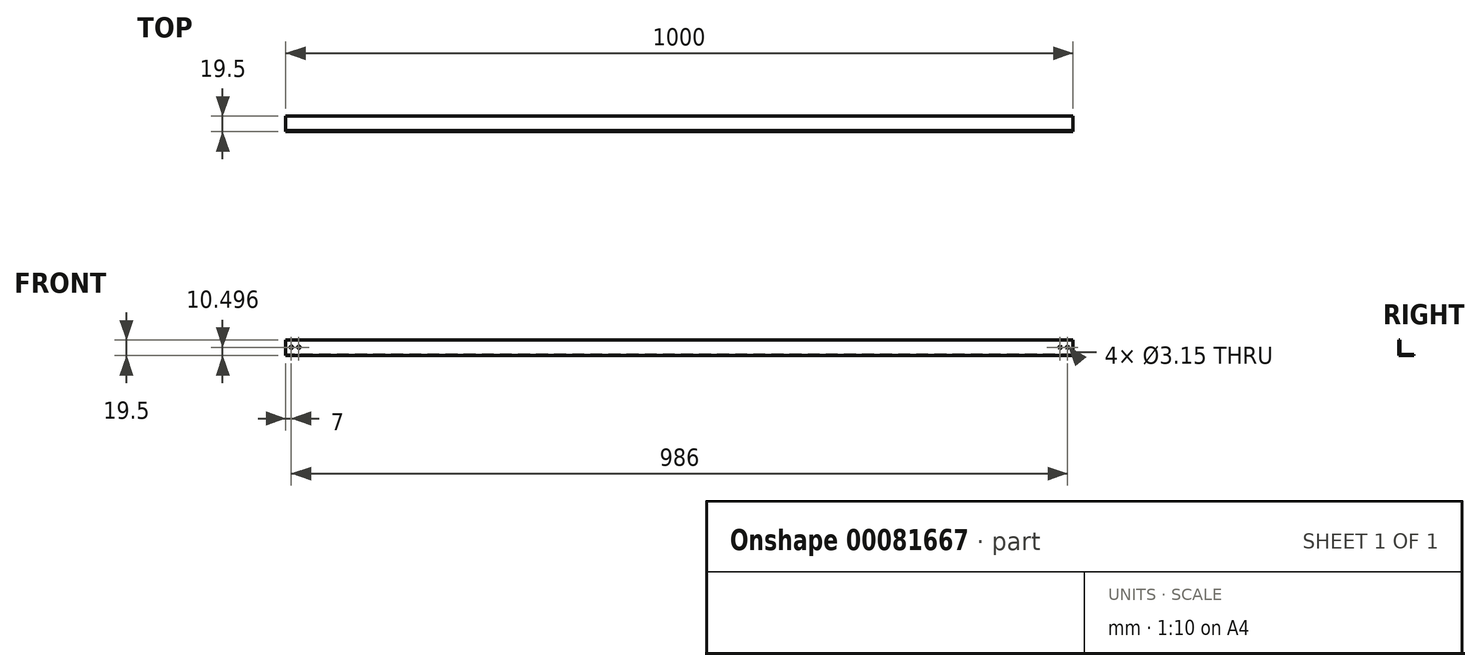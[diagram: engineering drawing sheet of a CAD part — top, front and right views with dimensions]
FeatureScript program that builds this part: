
annotation { "Feature Type Name" : "Feature", "Feature Type Description" : "" }
export const myFeature = defineFeature(function(context is Context, id is Id, definition is map)
    precondition{}
    {
        {
            var Q0;
            Q0=qCreatedBy(makeId("Right.planeOp"),FACE);
            var sketch = newSketch(context, id + "F0", { "sketchPlane" : qUnion([Q0])});
            skLineSegment(sketch, "E0.bottom", {"start": v(0.07, 7.23) * mm, "end": v(19.57, 7.23) * mm});
            skLineSegment(sketch, "E0.top", {"start": v(0.07, 5.73) * mm, "end": v(19.57, 5.73) * mm});
            skLineSegment(sketch, "E0.left", {"start": v(0.07, 7.23) * mm, "end": v(0.07, 5.73) * mm});
            skLineSegment(sketch, "E0.right", {"start": v(19.57, 7.23) * mm, "end": v(19.57, 5.73) * mm});
            skLineSegment(sketch, "E1.top", {"start": v(0.07, 25.23) * mm, "end": v(1.57, 25.23) * mm});
            skLineSegment(sketch, "E1.left", {"start": v(0.07, 7.23) * mm, "end": v(0.07, 25.23) * mm});
            skLineSegment(sketch, "E1.right", {"start": v(1.57, 7.23) * mm, "end": v(1.57, 25.23) * mm});
            skLineSegment(sketch, "E2.bottom", {"start": v(19.57, 7.23) * mm, "end": v(18.07, 7.23) * mm});
            skLineSegment(sketch, "E2.top", {"start": v(19.57, 25.23) * mm, "end": v(18.07, 25.23) * mm});
            skLineSegment(sketch, "E2.left", {"start": v(19.57, 7.23) * mm, "end": v(19.57, 25.23) * mm});
            skLineSegment(sketch, "E2.right", {"start": v(18.07, 7.23) * mm, "end": v(18.07, 25.23) * mm});
            skSolve(sketch);
        }
        {
            var Q0;
            Q0=makeQuery(id+"F0.imprint","IMPRINT",FACE,{"disambiguationData":[TD([[makeQuery(id+"F0.imprint","IMPRINT",EDGE,{"derivedFrom":sQuery(id+"F0.wireOp",EDGE,"E1.top")}),-1.0]])]});
            var Q1;
            Q1=makeQuery(id+"F0.imprint","IMPRINT",FACE,{"disambiguationData":[TD([[makeQuery(id+"F0.imprint","IMPRINT",EDGE,{"derivedFrom":sQuery(id+"F0.wireOp",EDGE,"E0.top")}),1.0]])]});
            var Q2;
            Q2=makeQuery(id+"F0.imprint","IMPRINT",FACE,{"disambiguationData":[TD([[makeQuery(id+"F0.imprint","IMPRINT",EDGE,{"derivedFrom":sQuery(id+"F0.wireOp",EDGE,"E2.bottom")}),-1.0]])]});
            extrude(context, id + "F1", {"entities" : qUnion([Q0, Q1, Q2]), "endBound" : BoundingType.SYMMETRIC, "depth" : 1000 * mm});
        }
        {
            var Q0;
            Q0=makeQuery(id+"F1.opExtrude","SWEPT_FACE",FACE,{"disambiguationData":[OSD([sQuery(id+"F0.wireOp",EDGE,"E1.right")])]});
            var sketch = newSketch(context, id + "F2", { "sketchPlane" : qUnion([Q0])});
            skLineSegment(sketch, "E3.bottom", {"start": v(500, 16.23) * mm, "end": v(493, 16.23) * mm});
            skLineSegment(sketch, "E3.top", {"start": v(500, 25.23) * mm, "end": v(493, 25.23) * mm});
            skLineSegment(sketch, "E3.left", {"start": v(500, 16.23) * mm, "end": v(500, 25.23) * mm});
            skLineSegment(sketch, "E3.right", {"start": v(493, 16.23) * mm, "end": v(493, 25.23) * mm});
            skLineSegment(sketch, "E4.bottom", {"start": v(493, 16.23) * mm, "end": v(483.5, 16.23) * mm});
            skLineSegment(sketch, "E4.top", {"start": v(493, 25.23) * mm, "end": v(483.5, 25.23) * mm});
            skLineSegment(sketch, "E4.right", {"start": v(483.5, 16.23) * mm, "end": v(483.5, 25.23) * mm});
            skLineSegment(sketch, "E5.bottom", {"start": v(-500, 16.23) * mm, "end": v(-493, 16.23) * mm});
            skLineSegment(sketch, "E5.top", {"start": v(-500, 25.23) * mm, "end": v(-493, 25.23) * mm});
            skLineSegment(sketch, "E5.left", {"start": v(-500, 16.23) * mm, "end": v(-500, 25.23) * mm});
            skLineSegment(sketch, "E5.right", {"start": v(-493, 16.23) * mm, "end": v(-493, 25.23) * mm});
            skLineSegment(sketch, "E6.bottom", {"start": v(-493, 16.23) * mm, "end": v(-483.5, 16.23) * mm});
            skLineSegment(sketch, "E6.top", {"start": v(-493, 25.23) * mm, "end": v(-483.5, 25.23) * mm});
            skLineSegment(sketch, "E6.right", {"start": v(-483.5, 16.23) * mm, "end": v(-483.5, 25.23) * mm});
            skCircle(sketch, "E7", {"center": v(493, 16.23) * mm, "radius": 1.6 * mm});
            skCircle(sketch, "E8", {"center": v(483.5, 16.23) * mm, "radius": 1.6 * mm});
            skCircle(sketch, "E9", {"center": v(-493, 16.23) * mm, "radius": 1.6 * mm});
            skCircle(sketch, "E10", {"center": v(-483.5, 16.23) * mm, "radius": 1.6 * mm});
            skSolve(sketch);
        }
        {
            var Q0;
            Q0=sQuery(id+"F2.wireOp",VERTEX,"E6.right.start");
            var Q1;
            Q1=sQuery(id+"F2.wireOp",VERTEX,"E5.right.start");
            var Q2;
            Q2=sQuery(id+"F2.wireOp",VERTEX,"E3.right.start");
            var Q3;
            Q3=sQuery(id+"F2.wireOp",VERTEX,"E4.right.start");
            var Q4;
            Q4=makeQuery(id+"F1.opExtrude","SWEPT_BODY",BODY,{"disambiguationData":[OSD([sQuery(id+"F0.wireOp",EDGE,"E0.bottom"),sQuery(id+"F0.wireOp",EDGE,"E0.top"),sQuery(id+"F0.wireOp",EDGE,"E0.left"),sQuery(id+"F0.wireOp",EDGE,"E0.right"),sQuery(id+"F0.wireOp",EDGE,"E1.top"),sQuery(id+"F0.wireOp",EDGE,"E1.left"),sQuery(id+"F0.wireOp",EDGE,"E1.right"),sQuery(id+"F0.wireOp",EDGE,"E2.top"),sQuery(id+"F0.wireOp",EDGE,"E2.left"),sQuery(id+"F0.wireOp",EDGE,"E2.right")])]});
            hole(context, id + "F3", {"style" : HoleStyle.SIMPLE, "endStyle" : HoleEndStyle.THROUGH, "standardTappedOrClearance" : lookupTablePath({ "standard" : "ISO", "fit" : "Close", "size" : "M3", "type" : "Clearance" }), "standardBlindInLast" : lookupTablePath({ "fit" : "Close", "standard" : "ISO", "size" : "M3", "type" : "Clearance" }), "holeDiameter" : 3.15 * mm, "locations" : qUnion([Q0, Q1, Q2, Q3]), "scope" : qUnion([Q4]), "isTappedThrough" : true});
        }
    });
